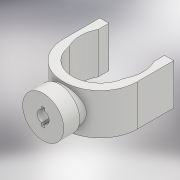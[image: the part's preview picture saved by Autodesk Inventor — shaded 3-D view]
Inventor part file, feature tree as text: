
AUTODESK INVENTOR PART (.ipt)
format: ipt  version: 2018.2 (Build 222227000, 227)  size: 196,608 bytes
history: native  units: mm
features: extrude x6, sketch x5, fillet x2
ambient origin geometry x8: Origin, YZ Plane, XZ Plane, XY Plane, X Axis, Y Axis, Z Axis, Center Point
bodies: Solid1 (feature_tree)
feature tree (13):
  extrude  "Extrusion1"  Depth=9.0mm
  extrude  "Extrusion5"  Depth=3.5mm
  extrude  "Extrusion6"  Depth=7.3mm
  extrude  "Extrusion2"  Depth=8.0mm TaperAngle=0.0deg
  sketch  "Sketch3"  dims[d7=18.0mm d8=0.0mm d9=7.3mm]
  extrude  "Extrusion3"  Depth=1.0mm
  extrude  "Extrusion4"  Depth=1.0mm
  fillet  "Fillet1"  Radius=0.26mm
  fillet  "Fillet2"  Radius=0.7mm
  sketch  "Sketch1"  dims[d1=2.1mm d3=9.0mm]
  sketch  "Sketch2"  dims[d4=3.5mm d5=0.0mm d6=2.0mm]
  sketch  "Sketch4"  dims[d10=2.0mm d11=8.0mm d12=0.0mm]
  sketch  "Sketch8"  dims[d13=12.0mm d14=0.0mm d15=1.0mm d16=1.0mm d18=0.26mm d19=0.7mm d20=3.75mm d23=2.0mm d24=9.0mm d25=8.0mm d26=13.75mm d27=2.5mm d28=9.0mm d29=0.0mm d33=8.0mm d34=9.0mm d35=0.0mm d36=12.2mm]
